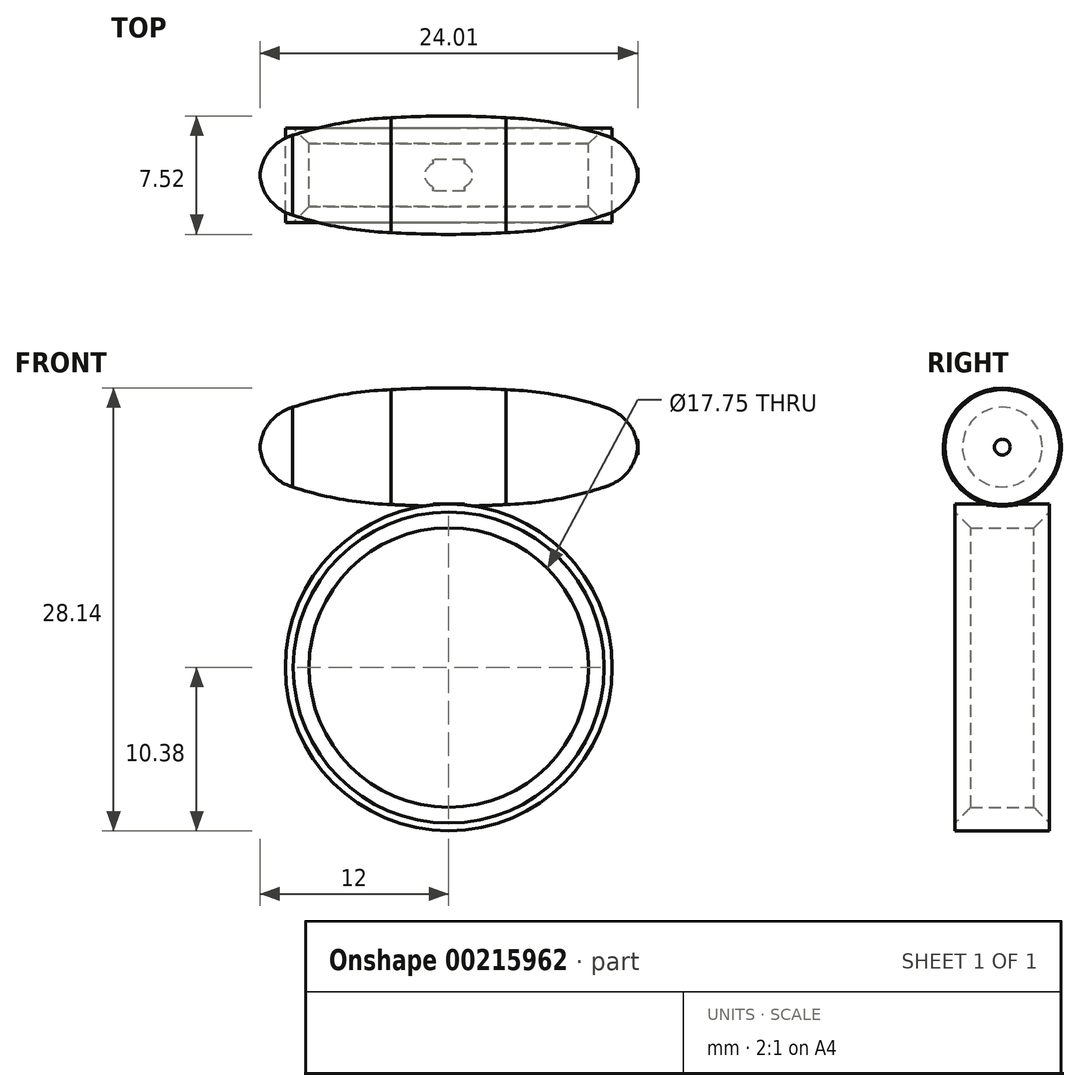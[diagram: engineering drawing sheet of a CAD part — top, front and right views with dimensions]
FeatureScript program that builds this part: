
annotation { "Feature Type Name" : "Feature", "Feature Type Description" : "" }
export const myFeature = defineFeature(function(context is Context, id is Id, definition is map)
    precondition{}
    {
        {
            var Q0;
            Q0=qCreatedBy(makeId("Front.planeOp"),FACE);
            var sketch = newSketch(context, id + "F0", { "sketchPlane" : qUnion([Q0])});
            skArc(sketch, "E0", {"start": v(10.17, -2.45) * mm, "mid": v(11.43, -1.48) * mm, "end": v(12, 0) * mm});
            skArc(sketch, "E1", {"start": v(9.9, -2.53) * mm, "mid": v(10.04, -2.5) * mm, "end": v(10.17, -2.45) * mm});
            skArc(sketch, "E2", {"start": v(3.65, -3.65) * mm, "mid": v(6.82, -3.32) * mm, "end": v(9.9, -2.53) * mm});
            skArc(sketch, "E3.MirrorCS", {"start": v(-9.9, -2.53) * mm, "mid": v(-10.04, -2.5) * mm, "end": v(-10.17, -2.45) * mm});
            skArc(sketch, "E4.MirrorCS", {"start": v(-3.65, -3.65) * mm, "mid": v(-6.82, -3.32) * mm, "end": v(-9.9, -2.53) * mm});
            skArc(sketch, "E5.MirrorCS", {"start": v(-10.17, -2.45) * mm, "mid": v(-11.43, -1.48) * mm, "end": v(-12, 0) * mm});
            skLineSegment(sketch, "E6", {"start": v(-12, 0) * mm, "end": v(12, 0) * mm});
            skCircle(sketch, "E7", {"center": v(0, -14) * mm, "radius": 8.88 * mm});
            skCircle(sketch, "E8.0", {"center": v(0, -14) * mm, "radius": 10.38 * mm});
            skCircle(sketch, "E9.0", {"center": v(0, -14) * mm, "radius": 9.88 * mm, "construction": true});
            skArc(sketch, "E10", {"start": v(-3.65, -3.65) * mm, "mid": v(0, -3.76) * mm, "end": v(3.65, -3.65) * mm});
            skSolve(sketch);
        }
        {
            var Q0;
            Q0=qCreatedBy(makeId("Right.planeOp"),FACE);
            var sketch = newSketch(context, id + "F1", { "sketchPlane" : qUnion([Q0])});
            skCircle(sketch, "E11", {"center": v(0, 0) * mm, "radius": 10.17 * mm});
            skSolve(sketch);
        }
        {
            var Q0;
            Q0=makeQuery(id+"F0.imprint","IMPRINT",FACE,{"disambiguationData":[TD([[makeQuery(id+"F0.imprint","IMPRINT",EDGE,{"derivedFrom":sQuery(id+"F0.wireOp",EDGE,"E0")}),1.0]])]});
            var Q1;
            {var subQ4=sQuery(id+"F0.wireOp",EDGE,"2wZglCvm-YMkz-JYAf-UKNb-zqlYzmtpqHZj");Q1=makeQuery(id+"F0.imprint","IMPRINT",FACE,{"disambiguationData":[TD([[makeQuery(id+"F0.imprint","IMPRINT",EDGE,{"derivedFrom":subQ4}),1.0]])]});}
            var Q2;
            {var subQ0=sQuery(id+"F0.wireOp",EDGE,"E10");var subQ1=sQuery(id+"F0.wireOp",EDGE,"E8.0");var subQ2=makeQuery(id+"F0.imprint","INTERSECT",VERTEX,{"disambiguationData":[OD(0.0)],"derivedFrom":[subQ1,subQ0]});Q2=makeQuery(id+"F0.imprint","IMPRINT",FACE,{"disambiguationData":[TD([[makeQuery(id+"F0.imprint","IMPRINT",EDGE,{"disambiguationData":[TD([[subQ2,1.0]])],"derivedFrom":subQ1}),1.0]])]});}
            var Q3;
            Q3=sQuery(id+"F1.wireOp",EDGE,"E11");
            revolve(context, id + "F2", {"entities" : qUnion([Q0, Q1, Q2]), "axis" : qUnion([Q3]), "revolveType" : RevolveType.FULL});
        }
        {
            var Q0;
            Q0=makeQuery(id+"F2.opRevolve","SWEPT_EDGE",EDGE,{"disambiguationData":[OSD([sQuery(id+"F0.wireOp",EDGE,"E1"),sQuery(id+"F0.wireOp",EDGE,"E2")])]});
            fillet(context, id + "F3", {"entities" : qUnion([Q0]), "radius" : 20 * mm, "tangentPropagation" : true, "allowEdgeOverflow" : false});
        }
        {
            var Q0;
            Q0=makeQuery(id+"F0.imprint","IMPRINT",FACE,{"disambiguationData":[TD([[makeQuery(id+"F0.imprint","IMPRINT",EDGE,{"derivedFrom":sQuery(id+"F0.wireOp",EDGE,"E7")}),-1.0]])]});
            var Q1;
            {var subQ0=sQuery(id+"F0.wireOp",EDGE,"E10");var subQ1=sQuery(id+"F0.wireOp",EDGE,"E8.0");var subQ2=makeQuery(id+"F0.imprint","INTERSECT",VERTEX,{"disambiguationData":[OD(0.0)],"derivedFrom":[subQ1,subQ0]});Q1=makeQuery(id+"F0.imprint","IMPRINT",FACE,{"disambiguationData":[TD([[makeQuery(id+"F0.imprint","IMPRINT",EDGE,{"disambiguationData":[TD([[subQ2,1.0]])],"derivedFrom":subQ1}),1.0]])]});}
            extrude(context, id + "F4", {"entities" : qUnion([Q0, Q1]), "operationType" : NewBodyOperationType.ADD, "depth" : 3 * mm, "hasSecondDirection" : true, "secondDirectionOppositeDirection" : true, "secondDirectionDepth" : 3 * mm});
        }
        {
            var Q0;
            Q0=makeQuery(id+"F4.opExtrude","CAP_EDGE",EDGE,{"disambiguationData":[OSD([sQuery(id+"F0.wireOp",EDGE,"E7")])],"isStart":false});
            var Q1;
            Q1=makeQuery(id+"F4.opExtrude","SWEPT_FACE",FACE,{"disambiguationData":[OSD([sQuery(id+"F0.wireOp",EDGE,"E7")])]});
            chamfer(context, id + "F5", {"entities" : qUnion([Q0, Q1]), "width" : 1 * mm, "tangentPropagation" : true});
        }
        {
            var Q0;
            Q0=qCreatedBy(makeId("Front.planeOp"),FACE);
            var sketch = newSketch(context, id + "F6", { "sketchPlane" : qUnion([Q0])});
            skLineSegment(sketch, "E12.bottom", {"start": v(1, -4.18) * mm, "end": v(-1, -4.18) * mm});
            skLineSegment(sketch, "E12.top", {"start": v(1, -3.28) * mm, "end": v(-1, -3.28) * mm});
            skLineSegment(sketch, "E12.left", {"start": v(1, -4.18) * mm, "end": v(1, -3.28) * mm});
            skLineSegment(sketch, "E12.right", {"start": v(-1, -4.18) * mm, "end": v(-1, -3.28) * mm});
            skPoint(sketch, "E12.middle", {"position": v(0, -3.73) * mm});
            skSolve(sketch);
        }
        {
            var Q0;
            Q0=makeQuery(id+"F6.imprint","IMPRINT",FACE,{"disambiguationData":[TD([[makeQuery(id+"F6.imprint","IMPRINT",EDGE,{"derivedFrom":sQuery(id+"F6.wireOp",EDGE,"E12.bottom")}),-1.0]])]});
            extrude(context, id + "F7", {"entities" : qUnion([Q0]), "operationType" : NewBodyOperationType.ADD, "depth" : 1 * mm, "hasSecondDirection" : true, "secondDirectionOppositeDirection" : true, "secondDirectionDepth" : 1 * mm});
        }
    });
